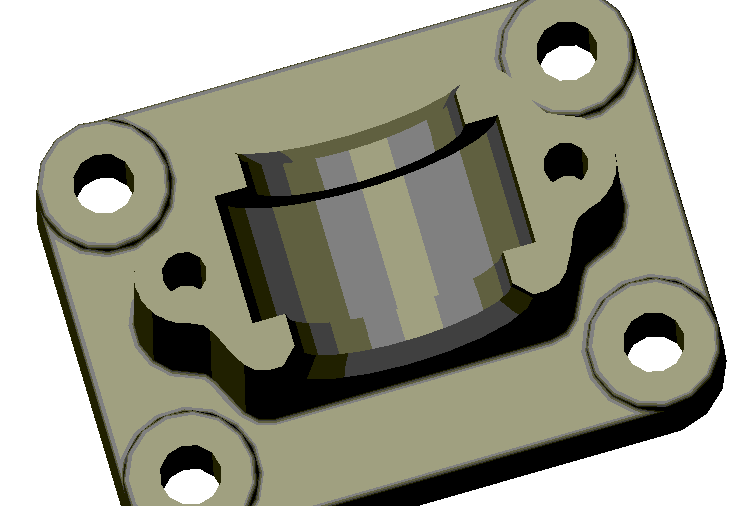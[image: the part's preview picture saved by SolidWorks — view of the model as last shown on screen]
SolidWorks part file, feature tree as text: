
SOLIDWORKS PART (.sldprt)
format: sldprt  version: not decoded by parser v0  size: 406,016 bytes
history: native  units: mm
features: sketch x8, fillet x5, plane x4, cut_extrude x4, extrude x3, pattern_linear x2, material x1, cut_revolve x1 + 1 further entry (+7 scaffold rows collapsed)
feature tree (36):
  scaffold x7  (default folders/planes/origin — collapsed)
  material  "Matériau <non spécifié>"
  "Corps de surface"
  plane  "Plan1"
  plane  "Plan2"
  plane  "Plan3"
  sketch  "Esquisse1"  dims[D3=12.5mm D1=110.0mm D2=80.0mm]
  extrude  "Base-Extrusion"  Depth=16mm
  sketch  "Esquisse2"
  extrude  "Boss.-Extru.1"  Depth=2mm
  pattern_linear  "Répétition linéaire2"  Count1=2 Count2=2 Spacing1=85mm Spacing2=55mm
  fillet  "Congé1"  Radius=1mm
  sketch  "Esquisse3"  dims[D1=11.0mm]
  cut_extrude  "Enlèv. mat.-Extru.1"  [1 undecoded]
  pattern_linear  "Répétition linéaire3"  Count1=2 Count2=2 Spacing1=85mm Spacing2=55mm
  fillet  "Congé3"  Radius=1mm
  plane  "Plan4"  Offset=51mm
  sketch  "Esquisse5"  dims[D1=70.0mm D3=18.0mm D5=5.0mm D2=42.0mm D4=70.0mm]
  extrude  "Boss.-Extru.3"  [1 undecoded]
  fillet  "Congé6"  Radius=1mm
  sketch  "Esquisse6"  dims[c1.D1=26.0mm c1.D2=24.0mm c1.D3=20.0mm c1.D4=~10.141402mm c2.D4=~29.47219deg c2.D5=~1.764484mm c2.D3=20.0mm c3.D4=6.0mm c3.D5=~8.222223mm c4.D5=45.0deg c4.D1=20.0mm c4.D3=26.0mm c5.D1=24.0mm c5.D2=26.0mm c5.D3=20.0mm]
  cut_revolve  "Enlever de la matière-Révolution1"  Angle=180deg
  sketch  "Esquisse7"  dims[D1=8.0mm]
  cut_extrude  "Enlèv. mat.-Extru.2"  Depth=25mm
  sketch  "Esquisse9"  dims[D2=5.0mm D1=14.0mm]
  cut_extrude  "Enlèv. mat.-Extru.3"  Depth=3mm
  sketch  "Esquisse10"  dims[D3=5.0mm D1=22.0mm D2=50.0mm D4=11.0mm D5=25.0mm]
  cut_extrude  "Enlèv. mat.-Extru.4"  Depth=14mm
  fillet  "Congé10"  Radius=4mm
  fillet  "Congé11"  Radius=2mm
decode coverage: 20 of 23 modeling features carry decoded parameters; 1 rows unclassified (native names shown)
note: ~ marks probable driven/reference dimensions
note: 2 parameter values undecoded
note: suppression state not decoded; provenance and decode notes live in map.json
